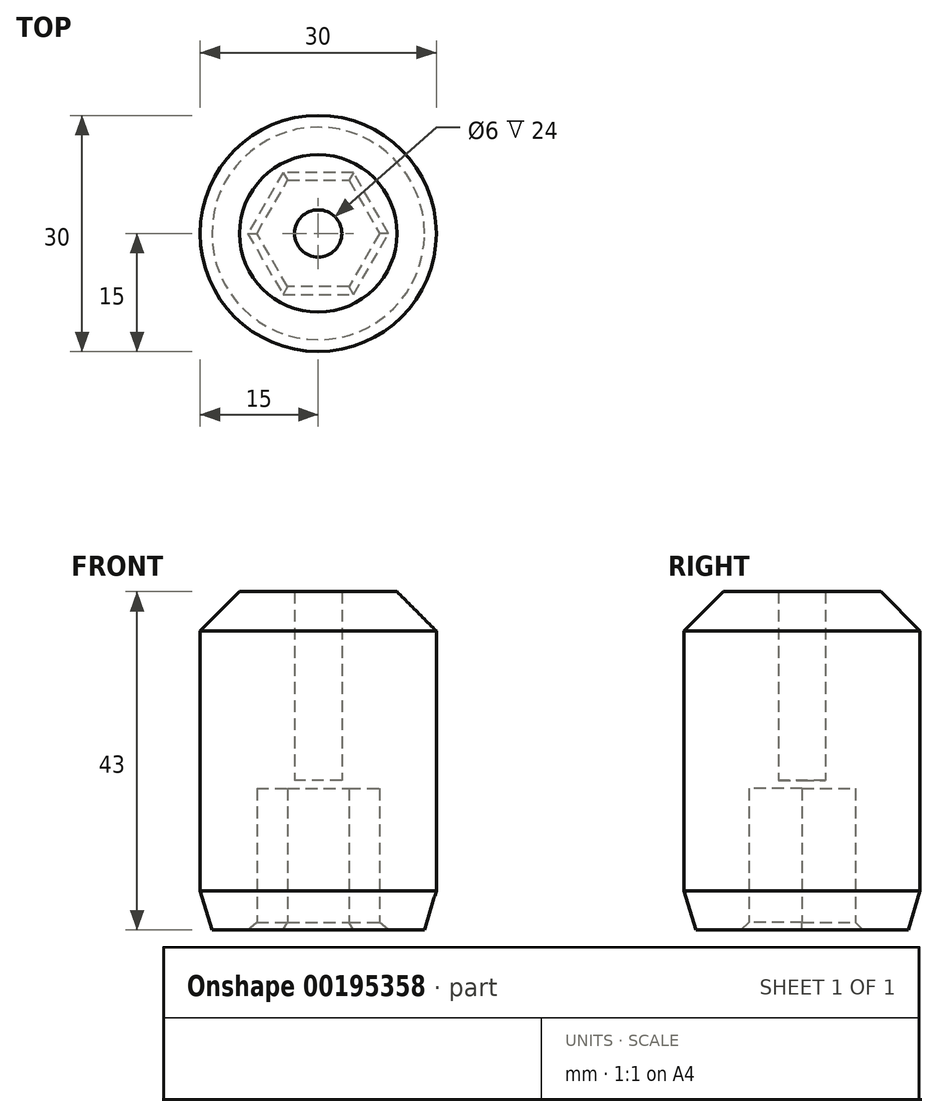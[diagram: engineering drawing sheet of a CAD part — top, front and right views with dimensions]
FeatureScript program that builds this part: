
annotation { "Feature Type Name" : "Feature", "Feature Type Description" : "" }
export const myFeature = defineFeature(function(context is Context, id is Id, definition is map)
    precondition{}
    {
        {
            var Q0;
            Q0=qCreatedBy(makeId("Top.planeOp"),FACE);
            var sketch = newSketch(context, id + "F0", { "sketchPlane" : qUnion([Q0])});
            skCircle(sketch, "E0", {"center": v(0, 0) * mm, "radius": 15 * mm});
            skCircle(sketch, "E1.cCircle", {"center": v(0, 0) * mm, "radius": 6.75 * mm, "construction": true});
            skLineSegment(sketch, "E1.0", {"start": v(-3.9, 6.75) * mm, "end": v(3.9, 6.75) * mm});
            skLineSegment(sketch, "E1.1", {"start": v(3.9, 6.75) * mm, "end": v(7.8, 0) * mm});
            skLineSegment(sketch, "E1.2", {"start": v(7.8, 0) * mm, "end": v(3.9, -6.75) * mm});
            skLineSegment(sketch, "E1.3", {"start": v(3.9, -6.75) * mm, "end": v(-3.9, -6.75) * mm});
            skLineSegment(sketch, "E1.4", {"start": v(-3.9, -6.75) * mm, "end": v(-7.8, 0) * mm});
            skLineSegment(sketch, "E1.5", {"start": v(-7.8, 0) * mm, "end": v(-3.9, 6.75) * mm});
            skPoint(sketch, "E1.0.midPoint", {"position": v(0, 6.75) * mm});
            skSolve(sketch);
        }
        {
            var Q0;
            Q0=makeQuery(id+"F0.imprint","IMPRINT",FACE,{"disambiguationData":[TD([[makeQuery(id+"F0.imprint","IMPRINT",EDGE,{"derivedFrom":sQuery(id+"F0.wireOp",EDGE,"E0")}),1.0]])]});
            extrude(context, id + "F1", {"entities" : qUnion([Q0]), "depth" : 18 * mm});
        }
        {
            var Q0;
            Q0=makeQuery(id+"F1.opExtrude","CAP_FACE",FACE,{"disambiguationData":[OSD([sQuery(id+"F0.wireOp",EDGE,"E0"),sQuery(id+"F0.wireOp",EDGE,"E1.0"),sQuery(id+"F0.wireOp",EDGE,"E1.1"),sQuery(id+"F0.wireOp",EDGE,"E1.2"),sQuery(id+"F0.wireOp",EDGE,"E1.3"),sQuery(id+"F0.wireOp",EDGE,"E1.4"),sQuery(id+"F0.wireOp",EDGE,"E1.5")])],"isStart":false});
            var sketch = newSketch(context, id + "F2", { "sketchPlane" : qUnion([Q0])});
            skCircle(sketch, "E2.0", {"center": v(0, 0) * mm, "radius": 15 * mm});
            skCircle(sketch, "E3", {"center": v(0, 0) * mm, "radius": 3 * mm});
            skSolve(sketch);
        }
        {
            var Q0;
            Q0=makeQuery(id+"F2.imprint","IMPRINT",FACE,{"disambiguationData":[TD([[makeQuery(id+"F2.imprint","IMPRINT",EDGE,{"derivedFrom":sQuery(id+"F2.wireOp",EDGE,"E2.0")}),1.0]])]});
            var Q1;
            Q1=makeQuery(id+"F2.imprint","IMPRINT",FACE,{"disambiguationData":[TD([[makeQuery(id+"F2.imprint","IMPRINT",EDGE,{"derivedFrom":sQuery(id+"F2.wireOp",EDGE,"E3")}),-1.0]])]});
            extrude(context, id + "F3", {"entities" : qUnion([Q0, Q1]), "operationType" : NewBodyOperationType.ADD, "depth" : 25 * mm});
        }
        {
            var Q0;
            Q0=makeQuery(id+"F3.opExtrude","CAP_EDGE",EDGE,{"disambiguationData":[OSD([sQuery(id+"F2.wireOp",EDGE,"E2.0")])],"isStart":false});
            chamfer(context, id + "F4", {"entities" : qUnion([Q0]), "width" : 5 * mm, "tangentPropagation" : true});
        }
        {
            var Q0;
            Q0=makeQuery(id+"F1.opExtrude","CAP_EDGE",EDGE,{"disambiguationData":[OSD([sQuery(id+"F0.wireOp",EDGE,"E1.3")])],"isStart":true});
            var Q1;
            Q1=makeQuery(id+"F1.opExtrude","CAP_EDGE",EDGE,{"disambiguationData":[OSD([sQuery(id+"F0.wireOp",EDGE,"E1.2")])],"isStart":true});
            var Q2;
            Q2=makeQuery(id+"F1.opExtrude","CAP_EDGE",EDGE,{"disambiguationData":[OSD([sQuery(id+"F0.wireOp",EDGE,"E1.1")])],"isStart":true});
            var Q3;
            Q3=makeQuery(id+"F1.opExtrude","CAP_EDGE",EDGE,{"disambiguationData":[OSD([sQuery(id+"F0.wireOp",EDGE,"E1.0")])],"isStart":true});
            var Q4;
            Q4=makeQuery(id+"F1.opExtrude","CAP_EDGE",EDGE,{"disambiguationData":[OSD([sQuery(id+"F0.wireOp",EDGE,"E1.5")])],"isStart":true});
            var Q5;
            Q5=makeQuery(id+"F1.opExtrude","CAP_EDGE",EDGE,{"disambiguationData":[OSD([sQuery(id+"F0.wireOp",EDGE,"E1.4")])],"isStart":true});
            chamfer(context, id + "F5", {"entities" : qUnion([Q0, Q1, Q2, Q3, Q4, Q5]), "width" : 1 * mm, "tangentPropagation" : true});
        }
        {
            var Q0;
            Q0=makeQuery(id+"F2.imprint","IMPRINT",FACE,{"disambiguationData":[TD([[makeQuery(id+"F2.imprint","IMPRINT",EDGE,{"derivedFrom":sQuery(id+"F2.wireOp",EDGE,"E3")}),1.0]])]});
            extrude(context, id + "F6", {"entities" : qUnion([Q0]), "operationType" : NewBodyOperationType.ADD, "depth" : 1 * mm});
        }
        {
            var Q0;
            Q0=makeQuery(id+"F1.opExtrude","CAP_EDGE",EDGE,{"disambiguationData":[OSD([sQuery(id+"F0.wireOp",EDGE,"E0")])],"isStart":true});
            chamfer(context, id + "F7", {"entities" : qUnion([Q0]), "chamferType" : ChamferType.TWO_OFFSETS, "width1" : 5 * mm, "oppositeDirection" : false, "width2" : 1.5 * mm, "tangentPropagation" : true});
        }
    });
